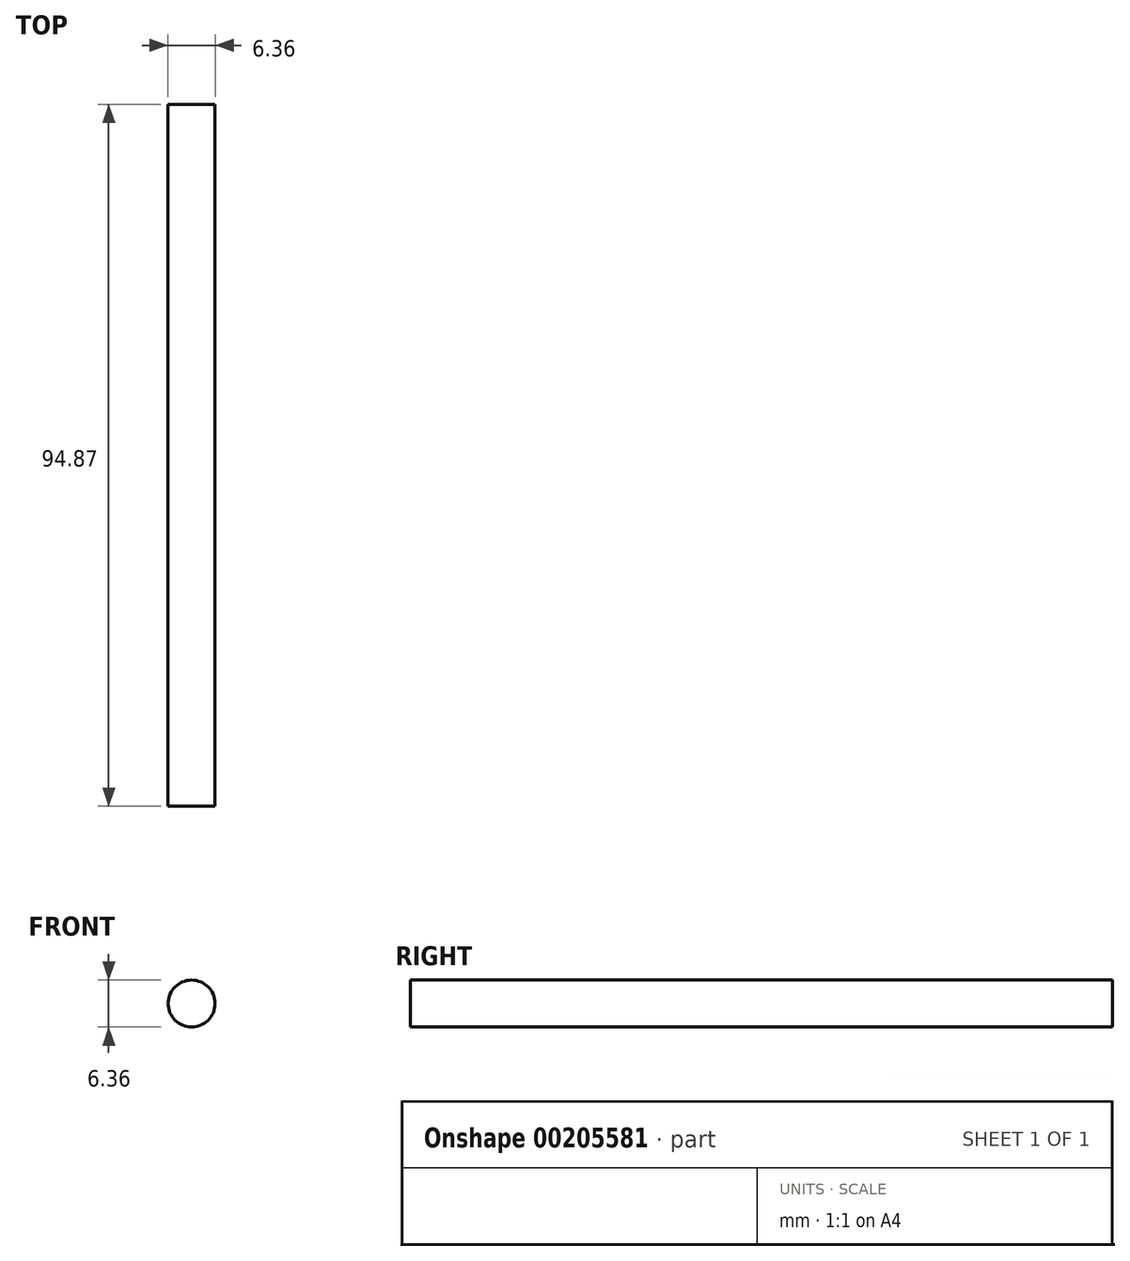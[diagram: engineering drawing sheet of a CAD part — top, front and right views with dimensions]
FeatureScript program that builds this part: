
annotation { "Feature Type Name" : "Feature", "Feature Type Description" : "" }
export const myFeature = defineFeature(function(context is Context, id is Id, definition is map)
    precondition{}
    {
        {
            var Q0;
            Q0=qCreatedBy(makeId("Front.planeOp"),FACE);
            var sketch = newSketch(context, id + "F0", { "sketchPlane" : qUnion([Q0])});
            skCircle(sketch, "E0", {"center": v(0, 0) * mm, "radius": 3.18 * mm});
            skSolve(sketch);
        }
        {
            var Q0;
            Q0=qSketchRegion(id+"F0",true);
            extrude(context, id + "F1", {"entities" : qUnion([Q0]), "flatOperationType" : FlatOperationType.REMOVE, "offsetDistance" : 25.4 * mm, "depth" : 94.87 * mm, "domain" : OperationDomain.MODEL});
        }
    });
